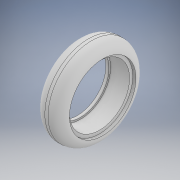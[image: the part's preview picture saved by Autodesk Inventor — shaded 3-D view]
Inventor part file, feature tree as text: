
AUTODESK INVENTOR PART (.ipt)
format: ipt  version: 2020 (Build 240168000, 168)  size: 165,376 bytes
history: native  units: mm
features: sketch x3, extrude x3, fillet x1
ambient origin geometry x8: Origin, YZ Plane, XZ Plane, XY Plane, X Axis, Y Axis, Z Axis, Center Point
bodies: Solid1 (feature_tree)
feature tree (7):
  sketch  "Sketch1"  dims[d0=27.5mm d1=19.0mm]
  sketch  "Sketch2"  dims[d2=5.0mm d3=21.0mm d4=6.0mm d5=0.0mm]
  extrude  "Extrusion1"  Depth=19.0mm
  extrude  "Extrusion2"  Depth=6.0mm
  fillet  "Fillet1"  Radius=6.0mm
  extrude  "Extrusion3"  Depth=3.5mm
  sketch  "Sketch3"  dims[d6=8.0mm d7=0.0mm d8=3.5mm d9=18.0mm d10=1.0mm d11=0.0mm]
